# Revit family: SL13
name_source: partatom
category: Plumbing Fixtures
revit_build: Autodesk Revit 2015 (Build: 20140606_1530(x64)
units: mm (PartAtom-declared; Revit-internal decimal feet)

## types (6) — shared parameters
Aluminium = Aluminum - Polished
Chrome = Chrome - Polished
Glass = Glass
Manufacturer = SanSwiss
Model = SL13
Seal = Seal
URL = http://www.sanswiss.com

## per-type parameters (varying)
| type | A | B | C | E | arm |
| 900 | 900 mm  [stored 2.95276 ft] | 277 mm  [stored 0.908793 ft] | 623 mm | 140 mm  [stored 0.459318 ft] | arm : 900 |
| 1000 | 1000 mm  [stored 3.28084 ft] | 377 mm  [stored 1.23688 ft] | 623 mm | 166 mm  [stored 0.544619 ft] | arm : 1000 |
| 800 | 800 mm  [stored 2.62467 ft] | 277 mm  [stored 0.908793 ft] | 523 mm | 140 mm  [stored 0.459318 ft] | arm : 800 |
| 1100 | 1100 mm | 277 mm  [stored 0.908793 ft] | 823 mm | 140 mm  [stored 0.459318 ft] | arm : 1000 |
| 1200 | 1200 mm | 377 mm  [stored 1.23688 ft] | 823 mm | 166 mm  [stored 0.544619 ft] | arm : 1200 |
| 1400 | 1400 mm  [stored 4.59318 ft] | 477 mm  [stored 1.56496 ft] | 923 mm | 192 mm  [stored 0.629921 ft] | arm : 1400 |

note: [stored X ft] marks values corroborated as IEEE doubles in the binary element streams (Revit-internal decimal feet)

## geometry (parser evidence)
native form markers: Sweep x15
no freeform markers — native parametric forms only
